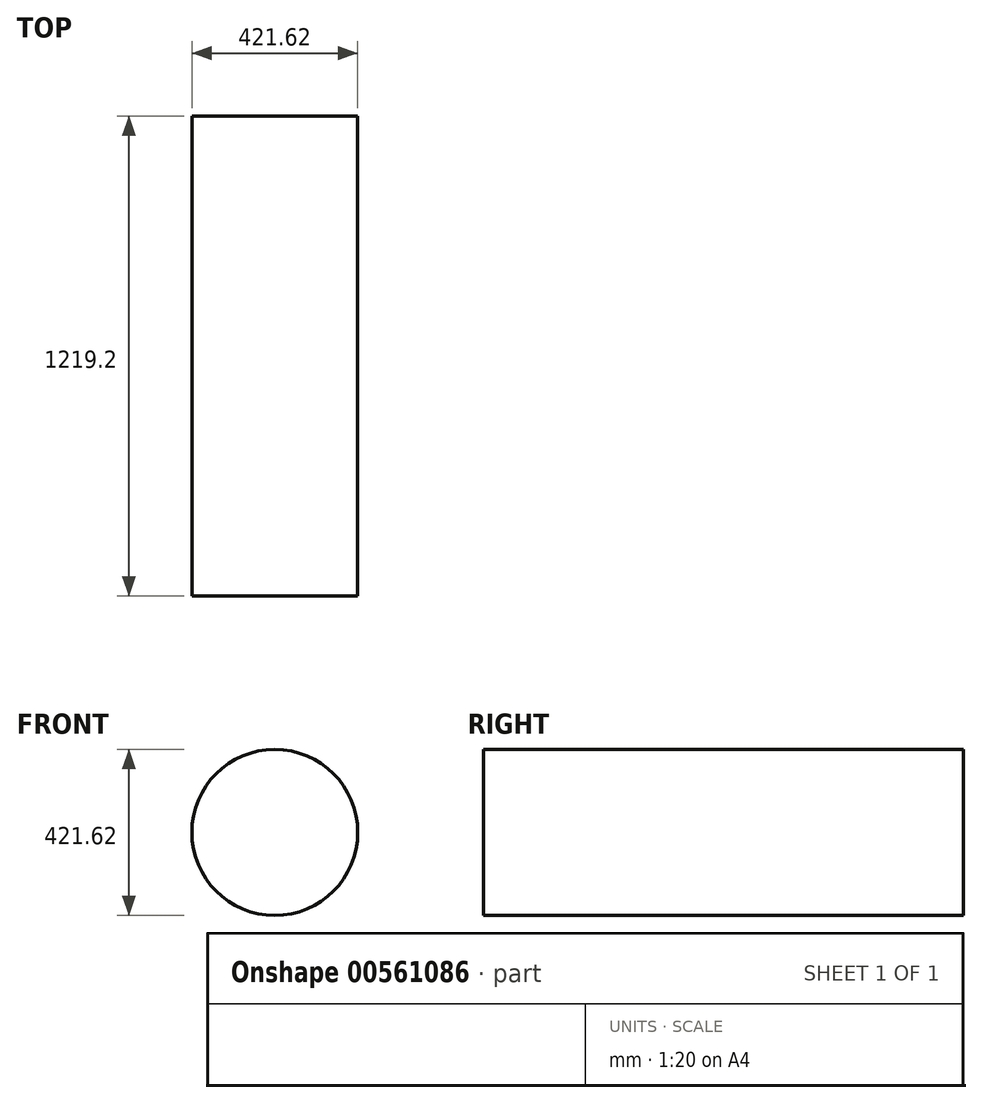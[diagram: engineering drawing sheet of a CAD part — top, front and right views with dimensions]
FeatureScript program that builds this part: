
annotation { "Feature Type Name" : "Feature", "Feature Type Description" : "" }
export const myFeature = defineFeature(function(context is Context, id is Id, definition is map)
    precondition{}
    {
        {
            var Q0;
            Q0=qCreatedBy(makeId("Front.planeOp"),FACE);
            var sketch = newSketch(context, id + "F0", { "sketchPlane" : qUnion([Q0])});
            skCircle(sketch, "E0", {"center": v(0, 0) * mm, "radius": 210.81 * mm});
            skSolve(sketch);
        }
        {
            var Q0;
            Q0 = qSketchRegion(id + "F0", true);
            extrude(context, id + "F1", {"entities" : qUnion([Q0]), "depth" : 1219.2 * mm, "offsetDistance" : 25.4 * mm});
        }
    });
